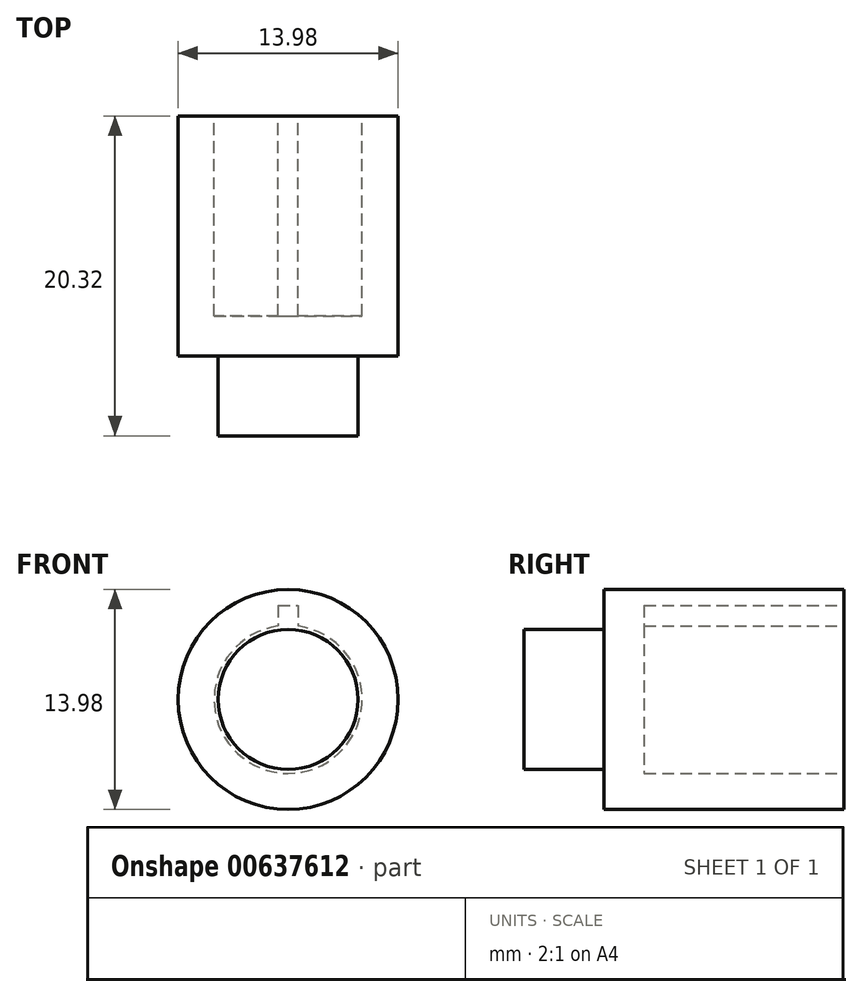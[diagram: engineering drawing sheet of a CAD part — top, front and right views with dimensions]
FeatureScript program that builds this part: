
annotation { "Feature Type Name" : "Feature", "Feature Type Description" : "" }
export const myFeature = defineFeature(function(context is Context, id is Id, definition is map)
    precondition{}
    {
        {
            var Q0;
            Q0=qCreatedBy(makeId("Front.planeOp"),FACE);
            var sketch = newSketch(context, id + "F0", { "sketchPlane" : qUnion([Q0])});
            skCircle(sketch, "E0", {"center": v(0, 0) * mm, "radius": 6.99 * mm});
            skCircle(sketch, "E1", {"center": v(0, 0) * mm, "radius": 4.7 * mm});
            skLineSegment(sketch, "E2", {"start": v(0, 4.7) * mm, "end": v(0, 5.97) * mm});
            skLineSegment(sketch, "E3", {"start": v(0, 5.97) * mm, "end": v(0.64, 5.97) * mm});
            skLineSegment(sketch, "E4", {"start": v(0.64, 5.97) * mm, "end": v(-0.64, 5.97) * mm});
            skLineSegment(sketch, "E5", {"start": v(-0.64, 5.97) * mm, "end": v(-0.64, 4.66) * mm});
            skLineSegment(sketch, "E6", {"start": v(0.64, 5.97) * mm, "end": v(0.64, 4.66) * mm});
            skSolve(sketch);
        }
        {
            var Q0;
            Q0=qSketchRegion(id+"F0",true);
            extrude(context, id + "F1", {"entities" : qUnion([Q0]), "depth" : 12.7 * mm});
        }
        {
            var Q0;
            Q0=makeQuery(id+"F1.opExtrude","CAP_FACE",FACE,{"disambiguationData":[OSD([sQuery(id+"F0.wireOp",EDGE,"E0"),sQuery(id+"F0.wireOp",EDGE,"E1"),sQuery(id+"F0.wireOp",EDGE,"E4"),sQuery(id+"F0.wireOp",EDGE,"E5"),sQuery(id+"F0.wireOp",EDGE,"E6")])],"isStart":false});
            var sketch = newSketch(context, id + "F2", { "sketchPlane" : qUnion([Q0])});
            skCircle(sketch, "E7", {"center": v(0, 0) * mm, "radius": 6.99 * mm});
            skSolve(sketch);
        }
        {
            var Q0;
            Q0=qSketchRegion(id+"F2",true);
            extrude(context, id + "F3", {"entities" : qUnion([Q0]), "operationType" : NewBodyOperationType.ADD, "depth" : 2.54 * mm});
        }
        {
            var Q0;
            Q0=makeQuery(id+"F3.opExtrude","CAP_FACE",FACE,{"disambiguationData":[OSD([sQuery(id+"F2.wireOp",EDGE,"E7")])],"isStart":false});
            var sketch = newSketch(context, id + "F4", { "sketchPlane" : qUnion([Q0])});
            skCircle(sketch, "E8", {"center": v(0, 0) * mm, "radius": 4.45 * mm});
            skSolve(sketch);
        }
        {
            var Q0;
            Q0=qSketchRegion(id+"F4",true);
            var Q1;
            Q1=makeQuery(id+"F4.imprint","IMPRINT",FACE,{"disambiguationData":[TD([[makeQuery(id+"F4.imprint","IMPRINT",EDGE,{"derivedFrom":sQuery(id+"F4.wireOp",EDGE,"E8")}),1.0]])]});
            extrude(context, id + "F5", {"entities" : qUnion([Q0, Q1]), "operationType" : NewBodyOperationType.ADD, "depth" : 5.08 * mm});
        }
    });
